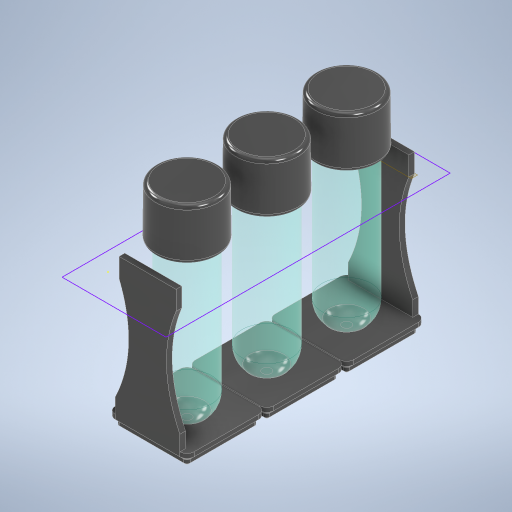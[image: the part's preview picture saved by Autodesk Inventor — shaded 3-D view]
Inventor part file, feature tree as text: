
AUTODESK INVENTOR PART (.ipt)
format: ipt  version: 2023 (Build 270158030, 158C)  size: 692,736 bytes
history: native  units: mm
features: sketch x12, other x11, extrude x11, plane x3, fillet x3, projected_geometry x3, pattern_linear x2, mirror x1
ambient origin geometry x8: Origin, YZ Plane, XZ Plane, XY Plane, X Axis, Y Axis, Z Axis, Center Point
bodies: Body1 (feature_tree), Body2 (feature_tree), Body3 (feature_tree), Body4 (feature_tree), Body5 (feature_tree), Body6 (feature_tree), Body7 (feature_tree)
feature tree (46):
  other  "rack"
  extrude  "base-generic"  Depth=41.5mm
  extrude  "Extrusion8"  Depth=2.25mm TaperAngle=0.0deg
  extrude  "Extrusion9"  Depth=2.15mm
  extrude  "Extrusion10"  Depth=0.8mm
  extrude  "Extrusion11"  Depth=7.75mm
  extrude  "Extrusion12"  Depth=7.75mm
  plane  "Work Plane3"
  extrude  "Extrusion15"  Depth=2.4mm TaperAngle=0.0deg
  fillet  "Fillet3"  Radius=3.0mm
  extrude  "Extrusion16"  Depth=30.0mm
  fillet  "Fillet4"  Radius=2.25mm
  extrude  "Extrusion17"  Depth=35.592094mm
  fillet  "Fillet5"  Radius=8.0mm
  pattern_linear  "Rectangular Pattern1"  Spacing1=2.0mm  [1 undecoded]
  extrude  "Extrusion18"  Depth=2.0mm
  pattern_linear  "Rectangular Pattern2"  Spacing1=13.0mm  [1 undecoded]
  plane  "Work Plane4"
  mirror  "Mirror1"
  plane  "Work Plane5"
  sketch  "Sketch22"  dims[d96=55.0mm d97=2.0mm d98=2.0mm d99=13.0mm d100=13.0mm d101=73.0mm d105=25.9mm d112=81.5mm d113=0.0mm d114=12.9mm d116=78.0mm d117=41.5mm d118=41.5mm d119=20.75mm d120=20.75mm d121=33.1mm d122=26.75mm d123=-0.087266mm d124=2.0mm d125=18.0mm d126=3.0mm d127=0.0mm d128=9.0mm d129=3.0mm d130=0.0mm d131=30.0mm d133=42.0mm d134=-10.0mm d17=0.5mm d18=0.872665mm d19=0.5mm d20=0.872665mm d24=0.0mm d25=0.0mm d26=0.0mm d27=0.0mm]
  extrude  "fill-gaps"  Depth=9.0mm
  sketch  "Sketch9"  dims[d50=41.5mm d51=41.5mm]
  sketch  "Sketch10"  dims[d52=3.75mm d53=2.25mm d54=0.0mm]
  projected_geometry  "Projected Loop2"
  sketch  "Sketch11"  dims[d55=3.75mm d56=2.15mm d57=-7.853982mm]
  projected_geometry  "Projected Loop3"
  sketch  "Sketch12"  dims[d58=1.8mm d59=0.0mm d60=0.8mm d61=-7.853982mm]
  projected_geometry  "Projected Loop4"
  sketch  "Sketch13"  dims[d62=6.5mm d63=7.75mm]
  sketch  "Sketch14"  dims[d64=7.75mm d65=7.75mm]
  sketch  "Sketch15"  dims[d66=7.75mm d67=2.4mm d68=0.0mm d69=3.0mm]
  sketch  "Sketch17"  dims[d70=6.0mm d71=0.0mm d72=30.0mm d74=42.0mm d75=10.0mm d77=42.0mm d79=2.25mm d80=0.0mm]
  sketch  "Sketch19"  dims[d82=3.75mm d84=35.592094mm d92=8.0mm]
  other  "test-tube"
  sketch  "Sketch20"  dims[d93=27.5mm]
  other  "tt-lid"
  sketch  "Sketch21"  dims[d95=10.0mm]
  other  "Pattern of test-tube:1"
  other  "TT-2"
  other  "Pattern of test-tube:2"
  other  "TT-3"
  other  "Pattern of tt-lid:3"
  other  "lid-2"
  other  "Pattern of tt-lid:4"
  other  "lid-3"
note: 2 required parameter values undecoded (feature->parameter linkage not recoverable at this tier; creation-order binding heuristic only, values carry confidence <= 0.55)
